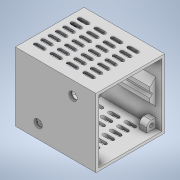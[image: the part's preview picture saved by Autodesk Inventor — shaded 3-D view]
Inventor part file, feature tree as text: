
AUTODESK INVENTOR PART (.ipt)
format: ipt  version: 2021 (Build 250183000, 183)  size: 602,112 bytes
history: native  units: mm
features: sketch x8, extrude x8, projected_geometry x5, plane x3, mirror x2, pattern_linear x1, fillet x1, hole x1
ambient origin geometry x8: Origin, YZ Plane, XZ Plane, XY Plane, X Axis, Y Axis, Z Axis, Center Point
bodies: Solid1 (feature_tree)
feature tree (29):
  sketch  "Sketch1"  dims[d0=75.0mm d1=75.0mm]
  extrude  "Extrusion1"  Depth=75.0mm
  extrude  "Extrusion2"  TaperAngle=45.0deg  [1 undecoded]
  sketch  "Sketch3"  dims[d2=3.0mm d4=45.0deg]
  plane  "Work Plane1"
  extrude  "Extrusion3"  Depth=60.5mm
  pattern_linear  "Rectangular Pattern1"  Spacing1=3.0mm  [1 undecoded]
  mirror  "Mirror1"
  extrude  "Extrusion4"  Depth=42.5mm
  plane  "Work Plane2"
  sketch  "Sketch7"  dims[d8=56.0mm]
  extrude  "Extrusion5"  [1 undecoded]
  extrude  "Extrusion6"  Depth=4.0mm
  plane  "Work Plane3"
  extrude  "Extrusion8"  Depth=5.0mm
  extrude  "Extrusion9"  Depth=15.0mm TaperAngle=0.0deg
  fillet  "Fillet2"  Radius=8.0mm
  mirror  "Mirror5"
  hole  "Hole1"  [1 undecoded]
  sketch  "Sketch5"  dims[d5=60.5mm d6=1.8mm]
  sketch  "Sketch6"  dims[d7=1.8mm]
  projected_geometry  "Projected Loop1"
  projected_geometry  "Projected Loop2"
  sketch  "Sketch8"  dims[d9=15.0mm]
  projected_geometry  "Projected Loop3"
  sketch  "Sketch9"  dims[d10=15.0mm]
  projected_geometry  "Projected Loop4"
  sketch  "Sketch10"  dims[d11=85.0mm d12=0.0mm d13=3.0mm d14=0.0mm d16=42.5mm d17=-7.853982mm d19=4.0mm d20=5.0mm d21=33.0mm d22=0.0mm d23=70.0mm d25=8.0mm d26=40.0mm d28=18.0mm d30=33.0mm d31=0.0mm d32=-6.5mm d33=4.3mm d34=5.0mm d35=5.0mm d36=7.2mm d37=8.0mm d38=0.0mm d39=4.0mm d40=0.0mm d41=5.0mm d42=5.0mm d43=7.2mm d44=4.3mm d48=3.0mm d49=3.0mm d50=3.0mm d51=4.0mm d52=0.0mm d54=15.0mm d55=7.5mm d57=4.3mm d58=5.0mm d59=0.0mm d60=5.0mm d61=7.5mm d62=15.0mm d63=4.3mm d64=61.5mm d65=14.0mm d66=9.0mm d67=6.0mm d68=15.0mm d69=9.0mm d70=90.0deg d71=10.0mm d72=20.594885mm d73=25.0mm d74=15.0mm d75=25.0mm d76=15.0mm]
  projected_geometry  "Projected Loop5"
note: 4 required parameter values undecoded (feature->parameter linkage not recoverable at this tier; creation-order binding heuristic only, values carry confidence <= 0.55)
